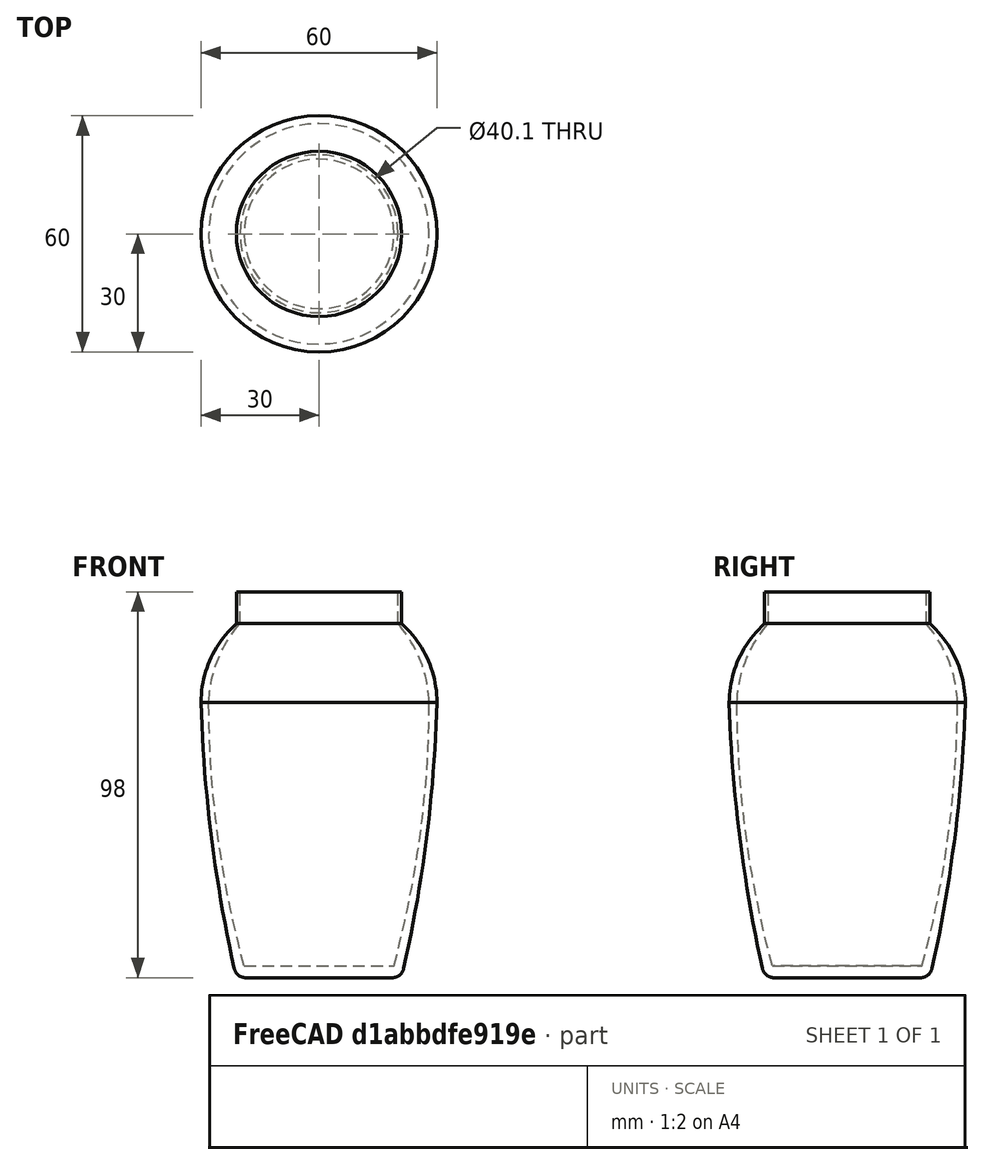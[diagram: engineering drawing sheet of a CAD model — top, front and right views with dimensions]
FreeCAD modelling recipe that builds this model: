
FCSTD DOCUMENT  (FreeCAD 0.20R29410 (Git))
Label: fit_long_millcco-cup
License: All rights reserved
LicenseURL: http://en.wikipedia.org/wiki/All_rights_reserved
objects: Part::Part2DObjectPython×12, Part::Feature×2, App::DocumentObjectGroup×2, Part::Revolution×2, Part::Cut×1, Part::Fillet×1
note: 18 computed .brp shape members not serialized (recipe doc carries the construction recipe); baked Part::Feature solids carry a one-line shape summary decoded from their .brp

FEATURE [Part::Part2DObjectPython] Line001  # Draft 2D object (typed FeaturePython)
  Area = 0
  ChamferSize = 0
  Closed = false
  End = (-21,0,-1.3e-15)
  FilletRadius = 0
  Length = 21
  MakeFace = true
  Placement = pos=(0,0,0) rot=(1,0,0;1.5708rad)
  Points = (2) [(0,0,0),(-21,-6.4294e-16,6.4294e-16)]
  Start = (0,0,0)
  Subdivisions = 0
FEATURE [Part::Part2DObjectPython] BSpline002  # Draft 2D object (typed FeaturePython)
  Area = 0
  Closed = false
  MakeFace = true
  Parameterization = 1
  Points = (3) [(-30,0,70),(-25,0,20),(-21,0,-1.28588e-15)]
FEATURE [Part::Part2DObjectPython] Line003  # Draft 2D object (typed FeaturePython)
  Area = 0
  ChamferSize = 0
  Closed = false
  End = (-21,0,98)
  FilletRadius = 0
  Length = 8
  MakeFace = true
  Placement = pos=(-22,0,90) rot=(1,0,0;1.5708rad)
  Points = (2) [(1,0,-3.06162e-17),(1,8,1.74574e-15)]
  Start = (-21,0,90)
  Subdivisions = 0
FEATURE [Part::Part2DObjectPython] Line004  # Draft 2D object (typed FeaturePython)
  Area = 0
  ChamferSize = 0
  Closed = false
  End = (0,0,98)
  FilletRadius = 0
  Length = 21
  MakeFace = true
  Placement = pos=(-22,0,95) rot=(1,0,0;1.5708rad)
  Points = (2) [(1,3,6.35518e-16),(22,3,-7.42192e-18)]
  Start = (-21,0,98)
  Subdivisions = 0
FEATURE [Part::Part2DObjectPython] Line005  # Draft 2D object (typed FeaturePython)
  Area = 0
  ChamferSize = 0
  Closed = false
  End = (0,0,0)
  FilletRadius = 0
  Length = 98
  MakeFace = true
  Placement = pos=(0,0,95) rot=(1,0,0;1.5708rad)
  Points = (2) [(9.18485e-17,3,6.66134e-16),(-2.90854e-15,-95,-2.10942e-14)]
  Start = (0,0,98)
  Subdivisions = 0
FEATURE [Part::Part2DObjectPython] BSpline  # Draft 2D object (typed FeaturePython)
  Area = 0
  Closed = false
  MakeFace = true
  Parameterization = 1
  Points = (3) [(-21,-3.69779e-32,90),(-28,0,80),(-30,0,70)]
FEATURE [Part::Part2DObjectPython] BSpline004  # Draft 2D object (typed FeaturePython)
  Area = 0
  Closed = false
  MakeFace = true
  Parameterization = 1
  Points = (3) [(-28,0,70),(-23,0,20),(-19,0,3)]
FEATURE [Part::Part2DObjectPython] Line007  # Draft 2D object (typed FeaturePython)
  Area = 0
  ChamferSize = 0
  Closed = false
  End = (0,6e-16,3)
  FilletRadius = 0
  Length = 19
  MakeFace = true
  Placement = pos=(-19,0,3) rot=(1,0,0;1.5708rad)
  Points = (2) [(0,0,0),(19,8.88178e-16,-5.81707e-16)]
  Start = (-19,0,3)
  Subdivisions = 0
FEATURE [Part::Part2DObjectPython] Line008  # Draft 2D object (typed FeaturePython)
  Area = 0
  ChamferSize = 0
  Closed = true
  End = (0,0,3)
  FilletRadius = 0
  Length = 95
  MakeFace = true
  Placement = pos=(0,0,95) rot=(1,0,0;1.5708rad)
  Points = (2) [(9.18485e-17,3,6.66134e-16),(-2.81669e-15,-92,-2.04281e-14)]
  Start = (0,0,98)
  Subdivisions = 0
FEATURE [Part::Part2DObjectPython] Line009  # Draft 2D object (typed FeaturePython)
  Area = 0
  ChamferSize = 0
  Closed = false
  End = (-20.05,0,90)
  FilletRadius = 0
  Length = 7.99864
  MakeFace = true
  Placement = pos=(-20.05,0,95) rot=(1,0,0;1.5708rad)
  Points = (2) [(-6.79016e-05,2.99864,6.65834e-16),(0,-5,-1.11022e-15)]
  Start = (-20.0501,0,97.9986)
  Subdivisions = 0
FEATURE [Part::Part2DObjectPython] BSpline005  # Draft 2D object (typed FeaturePython)
  Area = 0
  Closed = false
  MakeFace = true
  Parameterization = 1
  Points = (3) [(-20.05,2.95823e-31,90),(-26,0,80),(-28,0,70)]
FEATURE [Part::Part2DObjectPython] Line  # Draft 2D object (typed FeaturePython)
  Area = 0
  ChamferSize = 0
  Closed = false
  End = (0,0,98)
  FilletRadius = 0
  Length = 20.0501
  MakeFace = true
  Placement = pos=(-20.0501,0,97.9986) rot=(1,0,0;1.5708rad)
  Points = (2) [(0,0,0),(20.0501,0.00135803,-6.13555e-16)]
  Start = (-20.0501,0,97.9986)
  Subdivisions = 0
FEATURE [Part::Feature] Face
  shape: bbox 41.09 x 2e-07 x 110.8 mm, 1 faces, 0 solids (baked)
FEATURE [App::DocumentObjectGroup] ____________001  label="外壁"
  Group = -> [BSpline002,Line004,Line001,BSpline,Line005,Line003,Face]
FEATURE [Part::Revolution] Revolve
  Angle = 360
  Axis = (0,0,1)
  Base = (0,0,0)
  FaceMakerClass = Part::FaceMakerBullseye
  Solid = true
  Source = -> Face
  Symmetric = false
FEATURE [Part::Feature] Face001
  shape: bbox 39.23 x 2e-07 x 107.4 mm, 1 faces, 0 solids (baked)
FEATURE [Part::Revolution] Revolve001
  Angle = 360
  Axis = (0,0,1)
  Base = (0,0,0)
  FaceMakerClass = Part::FaceMakerBullseye
  Solid = true
  Source = -> Face001
  Symmetric = false
FEATURE [Part::Cut] Cut
  Base = -> Revolve
  Tool = -> Revolve001
FEATURE [App::DocumentObjectGroup] ____________  label="内壁"
  Group = -> [BSpline004,Line007,Line008,Line009,BSpline005,Line,Face001,Cut]
FEATURE [Part::Fillet] Fillet
  Base = -> Cut
  Edges = 1 edges r=3: [Edge1]
